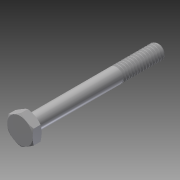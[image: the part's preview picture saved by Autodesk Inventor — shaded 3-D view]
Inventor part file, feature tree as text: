
AUTODESK INVENTOR PART (.ipt)
format: ipt  version: 2014 SP1 (Build 180222100, 222)  size: 509,952 bytes
history: native  units: in
note: dims shown in document units (in); Inventor stores cm internally (conversion verified against a paired STEP export)
features: extrude x1, other x1, imported_body x1
ambient origin geometry x8: Origin, YZ Plane, XZ Plane, XY Plane, X Axis, Y Axis, Z Axis, Center Point
bodies: Body1 (feature_tree)
feature tree (3):
  extrude  "Extrude14"  [1 undecoded]
  other  "91257A5511"
  imported_body  "Base1"
note: 1 required parameter value undecoded (feature->parameter linkage not recoverable at this tier; creation-order binding heuristic only, values carry confidence <= 0.55)
